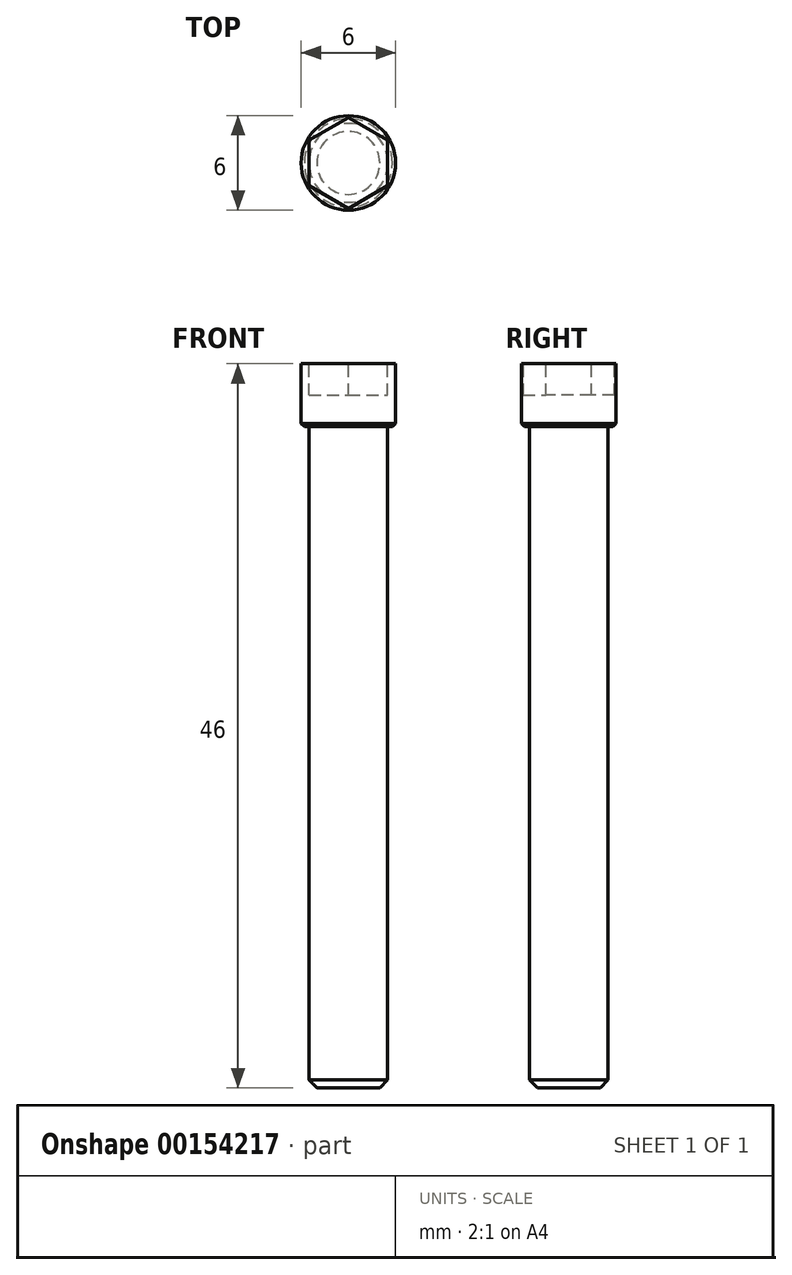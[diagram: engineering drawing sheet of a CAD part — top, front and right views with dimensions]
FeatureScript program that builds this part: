
annotation { "Feature Type Name" : "Feature", "Feature Type Description" : "" }
export const myFeature = defineFeature(function(context is Context, id is Id, definition is map)
    precondition{}
    {
        {
            var Q0;
            Q0=qCreatedBy(makeId("Top.planeOp"),FACE);
            var sketch = newSketch(context, id + "F0", { "sketchPlane" : qUnion([Q0])});
            skCircle(sketch, "E0", {"center": v(0, 0) * mm, "radius": 3 * mm});
            skSolve(sketch);
        }
        {
            var Q0;
            Q0 = qSketchRegion(id + "F0", true);
            extrude(context, id + "F1", {"entities" : qUnion([Q0]), "depth" : 4 * mm});
        }
        {
            var Q0;
            Q0=makeQuery(id+"F1.opExtrude","CAP_FACE",FACE,{"disambiguationData":[OSD([sQuery(id+"F0.wireOp",EDGE,"E0")])],"isStart":false});
            var sketch = newSketch(context, id + "F2", { "sketchPlane" : qUnion([Q0])});
            skCircle(sketch, "E1.cCircle", {"center": v(0, 0) * mm, "radius": 2.5 * mm, "construction": true});
            skLineSegment(sketch, "E1.0", {"start": v(2.5, 1.44) * mm, "end": v(2.5, -1.44) * mm});
            skLineSegment(sketch, "E1.1", {"start": v(2.5, -1.44) * mm, "end": v(0, -2.89) * mm});
            skLineSegment(sketch, "E1.2", {"start": v(0, -2.89) * mm, "end": v(-2.5, -1.44) * mm});
            skLineSegment(sketch, "E1.3", {"start": v(-2.5, -1.44) * mm, "end": v(-2.5, 1.44) * mm});
            skLineSegment(sketch, "E1.4", {"start": v(-2.5, 1.44) * mm, "end": v(0, 2.89) * mm});
            skLineSegment(sketch, "E1.5", {"start": v(0, 2.89) * mm, "end": v(2.5, 1.44) * mm});
            skPoint(sketch, "E1.0.midPoint", {"position": v(2.5, 0) * mm});
            skSolve(sketch);
        }
        {
            var Q0;
            Q0 = qSketchRegion(id + "F2", true);
            extrude(context, id + "F3", {"entities" : qUnion([Q0]), "operationType" : NewBodyOperationType.REMOVE, "oppositeDirection" : true, "depth" : 2 * mm});
        }
        {
            var Q0;
            Q0=makeQuery(id+"F1.opExtrude","CAP_FACE",FACE,{"disambiguationData":[OSD([sQuery(id+"F0.wireOp",EDGE,"E0")])],"isStart":true});
            var sketch = newSketch(context, id + "F4", { "sketchPlane" : qUnion([Q0])});
            skCircle(sketch, "E2", {"center": v(0, 0) * mm, "radius": 2.5 * mm});
            skSolve(sketch);
        }
        {
            var Q0;
            Q0 = qSketchRegion(id + "F4", true);
            extrude(context, id + "F5", {"entities" : qUnion([Q0]), "operationType" : NewBodyOperationType.ADD, "depth" : 42 * mm});
        }
        {
            var Q0;
            Q0=makeQuery(id+"F5.opExtrude","CAP_EDGE",EDGE,{"disambiguationData":[OSD([sQuery(id+"F4.wireOp",EDGE,"E2")])],"isStart":false});
            chamfer(context, id + "F6", {"entities" : qUnion([Q0]), "width" : 0.5 * mm, "tangentPropagation" : true});
        }
        {
            var Q0;
            Q0=makeQuery(id+"F1.opExtrude","CAP_EDGE",EDGE,{"disambiguationData":[OSD([sQuery(id+"F0.wireOp",EDGE,"E0")])],"isStart":true});
            chamfer(context, id + "F7", {"entities" : qUnion([Q0]), "width" : 0.2 * mm, "tangentPropagation" : true});
        }
    });
